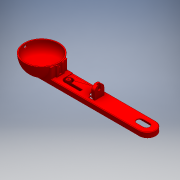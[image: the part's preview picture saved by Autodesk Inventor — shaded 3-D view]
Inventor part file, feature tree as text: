
AUTODESK INVENTOR PART (.ipt)
format: ipt  version: 2016 (Build 200138000, 138)  size: 471,040 bytes
history: native  units: mm
features: extrude x25, sketch x25, fillet x3, revolve x1, plane x1, thread x1
ambient origin geometry x8: Origin, YZ Plane, XZ Plane, XY Plane, X Axis, Y Axis, Z Axis, Center Point
bodies: Solid1 (feature_tree)
feature tree (56):
  revolve  "Revolution1"  [1 undecoded]
  plane  "Work Plane1"
  extrude  "Extrusion1"  Depth=12.5mm
  extrude  "Extrusion2"  Depth=3.0mm
  extrude  "Extrusion3"  Depth=10.0mm TaperAngle=0.0deg
  extrude  "Extrusion4"  Depth=2.0mm
  extrude  "Extrusion5"  Depth=2.0mm
  extrude  "Extrusion6"  Depth=9.0mm TaperAngle=0.0deg
  extrude  "Extrusion7"  Depth=2.0mm
  extrude  "Extrusion8"  Depth=5.75mm
  extrude  "Extrusion9"  Depth=1.5mm
  extrude  "Extrusion10"  Depth=1.0mm TaperAngle=0.0deg
  extrude  "Extrusion11"  Depth=3.5mm
  extrude  "Extrusion12"  Depth=1.0mm TaperAngle=0.0deg
  extrude  "Extrusion13"  Depth=2.0mm TaperAngle=0.0deg
  extrude  "Extrusion14"  Depth=4.0mm
  thread  "Thread1"  [1 undecoded]
  extrude  "Extrusion15"  Depth=8.0mm TaperAngle=0.0deg
  extrude  "Extrusion16"  Depth=14.0mm
  extrude  "Extrusion17"  Depth=23.5mm
  extrude  "Extrusion18"  Depth=7.0mm TaperAngle=0.0deg
  extrude  "Extrusion19"  Depth=8.0mm TaperAngle=0.0deg
  extrude  "Extrusion20"  Depth=6.0mm TaperAngle=0.0deg
  extrude  "Extrusion21"  Depth=10.0mm
  extrude  "Extrusion22"  Depth=55.0mm
  extrude  "Extrusion23"  Depth=15.0mm
  extrude  "Extrusion24"  Depth=0.75mm
  extrude  "Extrusion25"  Depth=0.75mm
  fillet  "Fillet1"  Radius=3.0mm
  fillet  "Fillet2"  Radius=14.0mm
  fillet  "Fillet3"  Radius=13.0mm
  sketch  "Sketch1"  dims[d2=90.0deg d3=26.6mm]
  sketch  "Sketch2"  dims[d5=12.5mm d6=26.0mm]
  sketch  "Sketch3"  dims[d10=2.0mm d11=3.0mm]
  sketch  "Sketch4"  dims[d12=10.0mm d13=0.0mm d14=0.5mm d15=0.0mm]
  sketch  "Sketch5"  dims[d16=15.0mm d17=2.0mm]
  sketch  "Sketch6"  dims[d18=7.0mm d19=2.0mm]
  sketch  "Sketch7"  dims[d20=147.0mm d21=0.0mm d22=9.0mm d23=0.0mm]
  sketch  "Sketch8"  dims[d26=147.0mm d27=0.0mm d28=2.0mm]
  sketch  "Sketch9"  dims[d29=8.0mm d30=0.0mm d31=5.75mm]
  sketch  "Sketch10"  dims[d32=5.75mm d33=1.5mm]
  sketch  "Sketch11"  dims[d34=1.5mm d35=1.0mm d36=0.0mm]
  sketch  "Sketch12"  dims[d37=15.0mm d38=3.5mm]
  sketch  "Sketch14"  dims[d39=3.5mm d40=1.0mm d41=0.0mm]
  sketch  "Sketch15"  dims[d42=1.5mm d43=2.0mm d44=0.0mm]
  sketch  "Sketch16"  dims[d45=4.0mm d46=4.0mm d47=2.0mm d48=0.0mm]
  sketch  "Sketch17"  dims[d49=14.0mm d53=8.0mm d54=0.0mm]
  sketch  "Sketch18"  dims[d57=23.5mm d58=14.0mm]
  sketch  "Sketch20"  dims[d59=12.0mm d60=23.5mm]
  sketch  "Sketch21"  dims[d61=4.0mm d62=7.0mm d63=0.0mm]
  sketch  "Sketch22"  dims[d64=7.0mm d65=8.0mm d66=0.0mm]
  sketch  "Sketch23"  dims[d67=2.0mm d68=6.0mm d69=0.0mm]
  sketch  "Sketch24"  dims[d70=10.0mm d71=0.0mm d72=6.0mm]
  sketch  "Sketch25"  dims[d73=0.5mm d74=0.0mm d75=55.0mm]
  sketch  "Sketch26"  dims[d76=6.0mm d77=15.0mm]
  sketch  "Sketch27"  dims[d81=0.5mm d82=0.0mm d83=7.0mm d84=7.0mm d85=3.0mm d86=14.0mm d87=0.0mm d88=13.0mm d89=2.0mm d90=0.0mm d91=84.5mm d92=0.0mm d93=7.0mm d94=0.0mm d95=5.0mm d96=0.0mm d97=2.5mm d98=0.0mm d99=2.5mm d100=0.0mm d102=10.0mm d104=2.0mm d105=0.0mm d106=0.75mm d107=0.0mm d108=1.0mm d109=0.75mm d110=0.75mm]
note: 2 required parameter values undecoded (feature->parameter linkage not recoverable at this tier; creation-order binding heuristic only, values carry confidence <= 0.55)